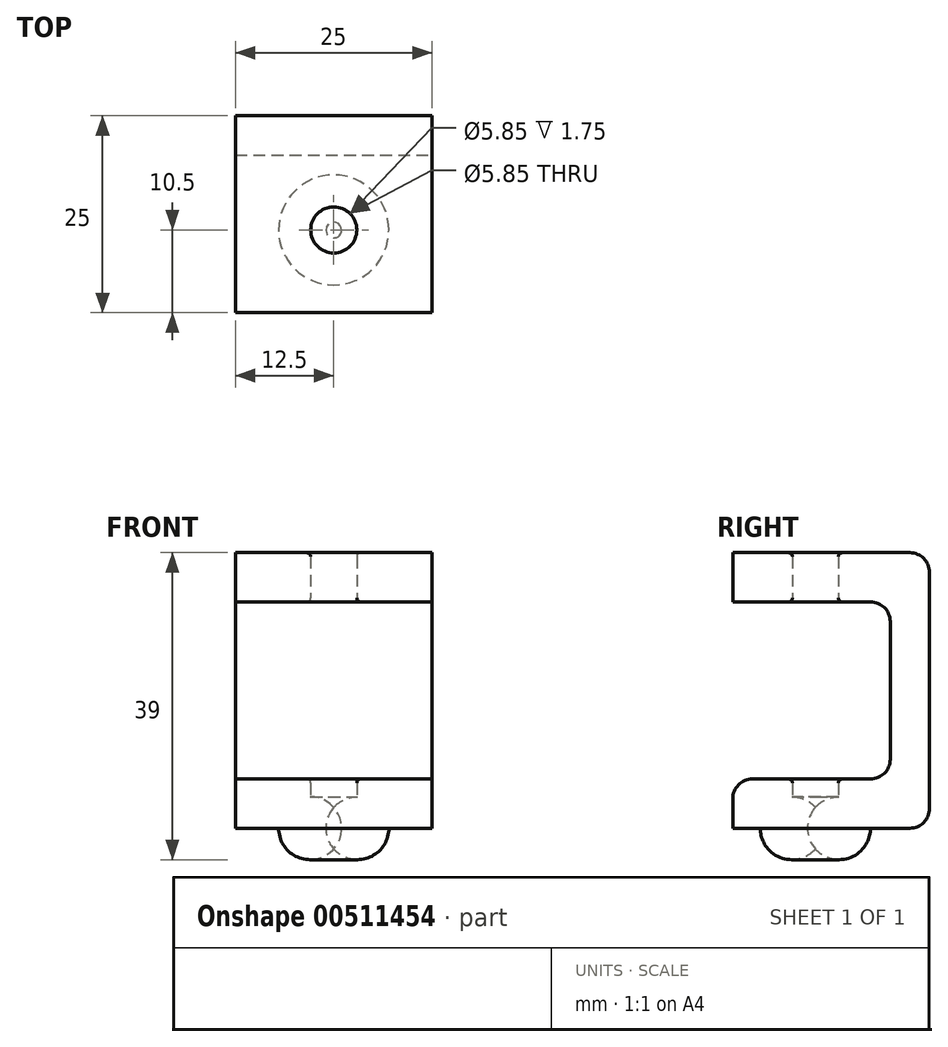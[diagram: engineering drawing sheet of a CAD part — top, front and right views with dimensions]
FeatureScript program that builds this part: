
annotation { "Feature Type Name" : "Feature", "Feature Type Description" : "" }
export const myFeature = defineFeature(function(context is Context, id is Id, definition is map)
    precondition{}
    {
        {
            var Q0;
            Q0=qCreatedBy(makeId("Top.planeOp"),FACE);
            var sketch = newSketch(context, id + "F0", { "sketchPlane" : qUnion([Q0])});
            skLineSegment(sketch, "E0.bottom", {"start": v(-12.5, -12.5) * mm, "end": v(12.5, -12.5) * mm});
            skLineSegment(sketch, "E0.top", {"start": v(-12.5, 12.5) * mm, "end": v(12.5, 12.5) * mm});
            skLineSegment(sketch, "E0.left", {"start": v(-12.5, -12.5) * mm, "end": v(-12.5, 12.5) * mm});
            skLineSegment(sketch, "E0.right", {"start": v(12.5, -12.5) * mm, "end": v(12.5, 12.5) * mm});
            skPoint(sketch, "E0.middle", {"position": v(0, 0) * mm});
            skLineSegment(sketch, "E1", {"start": v(0, -12.5) * mm, "end": v(0, 0) * mm, "construction": true});
            skCircle(sketch, "E2", {"center": v(0, -2) * mm, "radius": 2.93 * mm});
            skCircle(sketch, "E3", {"center": v(0, -2) * mm, "radius": 7 * mm});
            skSolve(sketch);
        }
        {
            var Q0;
            Q0=makeQuery(id+"F0.imprint","IMPRINT",FACE,{"disambiguationData":[TD([[makeQuery(id+"F0.imprint","IMPRINT",EDGE,{"derivedFrom":sQuery(id+"F0.wireOp",EDGE,"E0.bottom")}),1.0]])]});
            var Q1;
            Q1=makeQuery(id+"F0.imprint","IMPRINT",FACE,{"disambiguationData":[TD([[makeQuery(id+"F0.imprint","IMPRINT",EDGE,{"derivedFrom":sQuery(id+"F0.wireOp",EDGE,"E2")}),-1.0]])]});
            var Q2;
            Q2=makeQuery(id+"F0.imprint","IMPRINT",FACE,{"disambiguationData":[TD([[makeQuery(id+"F0.imprint","IMPRINT",EDGE,{"derivedFrom":sQuery(id+"F0.wireOp",EDGE,"E2")}),1.0]])]});
            extrude(context, id + "F1", {"entities" : qUnion([Q0, Q1, Q2]), "depth" : 35 * mm, "offsetDistance" : 25 * mm});
        }
        {
            var Q0;
            Q0=makeQuery(id+"F1.opExtrude","SWEPT_FACE",FACE,{"disambiguationData":[OSD([sQuery(id+"F0.wireOp",EDGE,"E0.bottom")])]});
            var sketch = newSketch(context, id + "F2", { "sketchPlane" : qUnion([Q0])});
            skLineSegment(sketch, "E4.bottom", {"start": v(-12.5, 6.25) * mm, "end": v(12.5, 6.25) * mm});
            skLineSegment(sketch, "E4.top", {"start": v(-12.5, 28.75) * mm, "end": v(12.5, 28.75) * mm});
            skLineSegment(sketch, "E4.left", {"start": v(-12.5, 6.25) * mm, "end": v(-12.5, 28.75) * mm});
            skLineSegment(sketch, "E4.right", {"start": v(12.5, 6.25) * mm, "end": v(12.5, 28.75) * mm});
            skPoint(sketch, "E4.middle", {"position": v(0, 17.5) * mm});
            skPoint(sketch, "E4.middle.positionSnap0", {"position": v(-12.5, 17.5) * mm});
            skPoint(sketch, "E4.centerSnap0", {"position": v(-12.5, 17.5) * mm});
            skSolve(sketch);
        }
        {
            var Q0;
            Q0=qSketchRegion(id+"F2",true);
            extrude(context, id + "F3", {"entities" : qUnion([Q0]), "operationType" : NewBodyOperationType.REMOVE, "oppositeDirection" : true, "depth" : 20 * mm, "offsetDistance" : 25 * mm});
        }
        {
            var Q0;
            Q0=makeQuery(id+"F0.imprint","IMPRINT",FACE,{"disambiguationData":[TD([[makeQuery(id+"F0.imprint","IMPRINT",EDGE,{"derivedFrom":sQuery(id+"F0.wireOp",EDGE,"E2")}),1.0]])]});
            var Q1;
            Q1=makeQuery(id+"F1.opExtrude","SWEPT_BODY",BODY,{"disambiguationData":[OSD([sQuery(id+"F0.wireOp",EDGE,"E0.bottom"),sQuery(id+"F0.wireOp",EDGE,"E0.top"),sQuery(id+"F0.wireOp",EDGE,"E0.left"),sQuery(id+"F0.wireOp",EDGE,"E0.right")])]});
            extrude(context, id + "F4", {"entities" : qUnion([Q0]), "operationType" : NewBodyOperationType.REMOVE, "endBound" : BoundingType.THROUGH_ALL, "depth" : 25 * mm, "endBoundEntityBody" : qUnion([Q1]), "offsetDistance" : 25 * mm});
        }
        {
            var Q0;
            Q0=makeQuery(id+"F1.opExtrude","CAP_FACE",FACE,{"disambiguationData":[OSD([sQuery(id+"F0.wireOp",EDGE,"E0.bottom"),sQuery(id+"F0.wireOp",EDGE,"E0.top"),sQuery(id+"F0.wireOp",EDGE,"E0.left"),sQuery(id+"F0.wireOp",EDGE,"E0.right")])],"isStart":true});
            var sketch = newSketch(context, id + "F5", { "sketchPlane" : qUnion([Q0])});
            skCircle(sketch, "E5.0", {"center": v(0, 2) * mm, "radius": 7 * mm});
            skSolve(sketch);
        }
        {
            var Q0;
            Q0=qSketchRegion(id+"F5",true);
            extrude(context, id + "F6", {"entities" : qUnion([Q0]), "operationType" : NewBodyOperationType.REMOVE, "oppositeDirection" : true, "depth" : 4 * mm, "offsetDistance" : 25 * mm});
        }
        {
            var Q0;
            Q0=makeQuery(id+"F3.boolean.opBoolean","COPY",EDGE,{"derivedFrom":makeQuery(id+"F3.opExtrude","CAP_EDGE",EDGE,{"disambiguationData":[OSD([sQuery(id+"F2.wireOp",EDGE,"E4.bottom")])],"isStart":false})});
            var Q1;
            Q1=makeQuery(id+"F3.boolean.opBoolean","COPY",EDGE,{"derivedFrom":makeQuery(id+"F3.opExtrude","CAP_EDGE",EDGE,{"disambiguationData":[OSD([sQuery(id+"F2.wireOp",EDGE,"E4.top")])],"isStart":false})});
            var Q2;
            Q2=makeQuery(id+"F1.opExtrude","CAP_EDGE",EDGE,{"disambiguationData":[OSD([sQuery(id+"F0.wireOp",EDGE,"E0.top")])],"isStart":false});
            var Q3;
            Q3=makeQuery(id+"F1.opExtrude","CAP_EDGE",EDGE,{"disambiguationData":[OSD([sQuery(id+"F0.wireOp",EDGE,"E0.top")])],"isStart":true});
            var Q4;
            Q4=makeQuery(id+"F3.boolean.opBoolean","COPY",EDGE,{"derivedFrom":makeQuery(id+"F3.opExtrude","CAP_EDGE",EDGE,{"disambiguationData":[OSD([sQuery(id+"F2.wireOp",EDGE,"E4.top")])],"isStart":true})});
            var Q5;
            Q5=makeQuery(id+"F3.boolean.opBoolean","COPY",EDGE,{"derivedFrom":makeQuery(id+"F3.opExtrude","CAP_EDGE",EDGE,{"disambiguationData":[OSD([sQuery(id+"F2.wireOp",EDGE,"E4.bottom")])],"isStart":true})});
            fillet(context, id + "F7", {"entities" : qUnion([Q0, Q1, Q2, Q3, Q4, Q5]), "tangentPropagation" : true, "radius" : 2.5 * mm, "defaultsChanged" : false, "vertexSettings" : [], "allowEdgeOverflow" : false});
        }
        {
            var Q0;
            Q0=makeQuery(id+"F6.boolean.opBoolean","COPY",EDGE,{"derivedFrom":makeQuery(id+"F6.opExtrude","CAP_EDGE",EDGE,{"disambiguationData":[OSD([sQuery(id+"F5.wireOp",EDGE,"E5.0")])],"isStart":false})});
            fillet(context, id + "F8", {"entities" : qUnion([Q0]), "tangentPropagation" : true, "radius" : 4 * mm, "defaultsChanged" : true, "vertexSettings" : [], "allowEdgeOverflow" : false});
        }
        {
            var Q0;
            Q0=makeQuery(id+"F4.boolean.opBoolean","INTERSECT",EDGE,{"derivedFrom":[makeQuery(id+"F1.opExtrude","CAP_FACE",FACE,{"disambiguationData":[OSD([sQuery(id+"F0.wireOp",EDGE,"E0.bottom"),sQuery(id+"F0.wireOp",EDGE,"E0.top"),sQuery(id+"F0.wireOp",EDGE,"E0.left"),sQuery(id+"F0.wireOp",EDGE,"E0.right")])],"isStart":false}),makeQuery(id+"F4.opExtrude","SWEPT_FACE",FACE,{"disambiguationData":[OSD([sQuery(id+"F0.wireOp",EDGE,"E2")])]})]});
            var Q1;
            Q1=makeQuery(id+"F4.boolean.opBoolean","INTERSECT",EDGE,{"derivedFrom":[makeQuery(id+"F3.boolean.opBoolean","COPY",FACE,{"derivedFrom":makeQuery(id+"F3.opExtrude","SWEPT_FACE",FACE,{"disambiguationData":[OSD([sQuery(id+"F2.wireOp",EDGE,"E4.top")])]})}),makeQuery(id+"F4.opExtrude","SWEPT_FACE",FACE,{"disambiguationData":[OSD([sQuery(id+"F0.wireOp",EDGE,"E2")])]})]});
            var Q2;
            Q2=makeQuery(id+"F8.opFillet","BLEND_EDGE",EDGE,{"blendedFrom":[makeQuery(id+"F6.boolean.opBoolean","COPY",EDGE,{"derivedFrom":makeQuery(id+"F6.opExtrude","CAP_EDGE",EDGE,{"disambiguationData":[OSD([sQuery(id+"F5.wireOp",EDGE,"E5.0")])],"isStart":false})}),makeQuery(id+"F4.boolean.opBoolean","COPY",FACE,{"disambiguationData":[TD([makeQuery(id+"F3.boolean.opBoolean","COPY",FACE,{"derivedFrom":makeQuery(id+"F3.opExtrude","SWEPT_FACE",FACE,{"disambiguationData":[OSD([sQuery(id+"F2.wireOp",EDGE,"E4.bottom")])]})})])],"derivedFrom":makeQuery(id+"F4.opExtrude","SWEPT_FACE",FACE,{"disambiguationData":[OSD([sQuery(id+"F0.wireOp",EDGE,"E2")])]})})],"blendedInto":[makeQuery(id+"F4.boolean.opBoolean","COPY",FACE,{"disambiguationData":[TD([makeQuery(id+"F3.boolean.opBoolean","COPY",FACE,{"derivedFrom":makeQuery(id+"F3.opExtrude","SWEPT_FACE",FACE,{"disambiguationData":[OSD([sQuery(id+"F2.wireOp",EDGE,"E4.bottom")])]})})])],"derivedFrom":makeQuery(id+"F4.opExtrude","SWEPT_FACE",FACE,{"disambiguationData":[OSD([sQuery(id+"F0.wireOp",EDGE,"E2")])]})})]});
            var Q3;
            Q3=makeQuery(id+"F4.boolean.opBoolean","INTERSECT",EDGE,{"derivedFrom":[makeQuery(id+"F3.boolean.opBoolean","COPY",FACE,{"derivedFrom":makeQuery(id+"F3.opExtrude","SWEPT_FACE",FACE,{"disambiguationData":[OSD([sQuery(id+"F2.wireOp",EDGE,"E4.bottom")])]})}),makeQuery(id+"F4.opExtrude","SWEPT_FACE",FACE,{"disambiguationData":[OSD([sQuery(id+"F0.wireOp",EDGE,"E2")])]})]});
            fillet(context, id + "F9", {"entities" : qUnion([Q0, Q1, Q2, Q3]), "tangentPropagation" : true, "radius" : .5 * mm, "defaultsChanged" : false, "vertexSettings" : [], "allowEdgeOverflow" : false});
        }
    });
